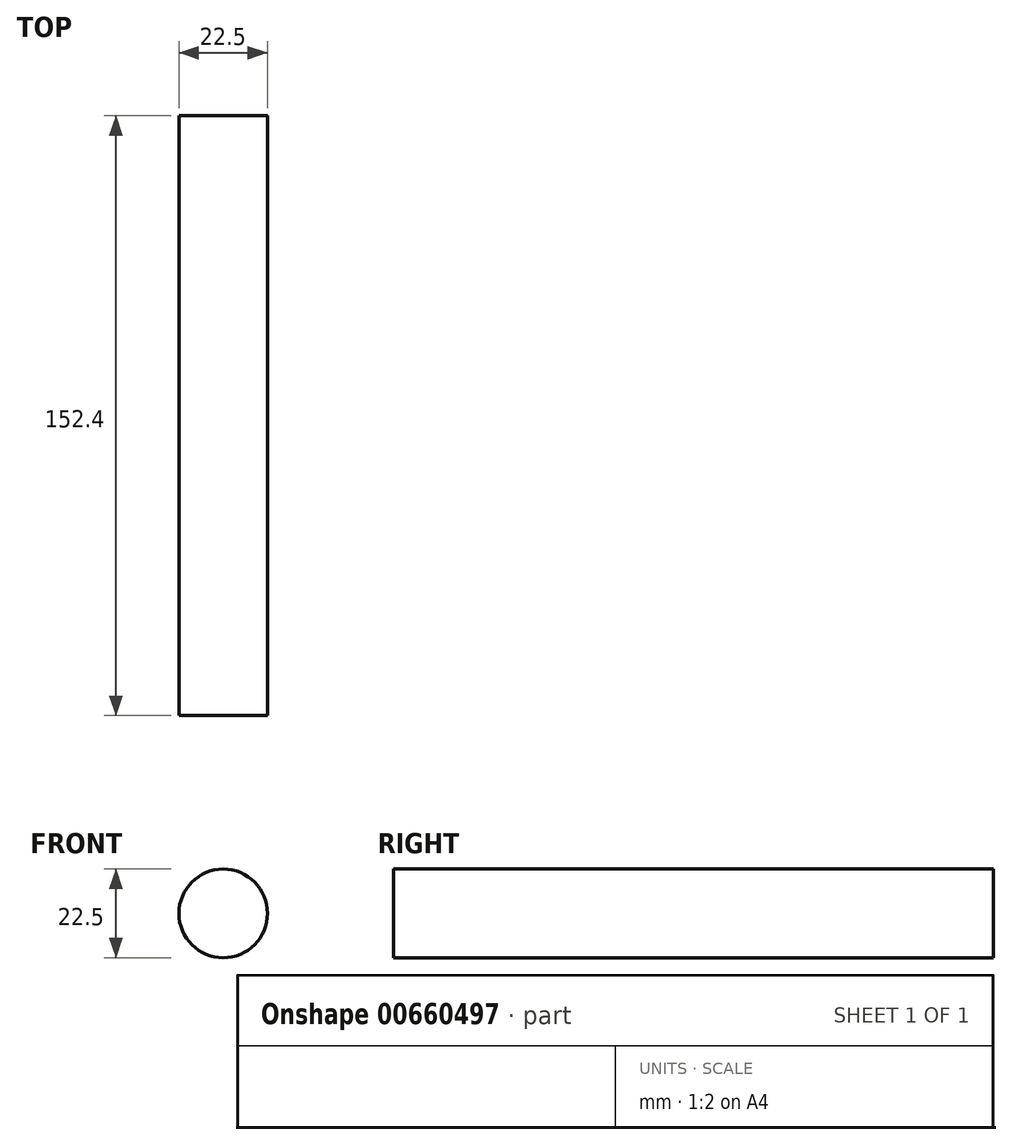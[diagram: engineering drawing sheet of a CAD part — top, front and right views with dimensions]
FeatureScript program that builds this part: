
annotation { "Feature Type Name" : "Feature", "Feature Type Description" : "" }
export const myFeature = defineFeature(function(context is Context, id is Id, definition is map)
    precondition{}
    {
        {
            var Q0;
            Q0=qCreatedBy(makeId("Front.planeOp"),FACE);
            var sketch = newSketch(context, id + "F0", { "sketchPlane" : qUnion([Q0])});
            skCircle(sketch, "E0", {"center": v(0, 0) * mm, "radius": 11.25 * mm});
            skSolve(sketch);
        }
        {
            var Q0;
            Q0=makeQuery(id+"F0.imprint","IMPRINT",FACE,{"disambiguationData":[TD([[makeQuery(id+"F0.imprint","IMPRINT",EDGE,{"derivedFrom":sQuery(id+"F0.wireOp",EDGE,"E0")}),1.0]])]});
            extrude(context, id + "F1", {"entities" : qUnion([Q0]), "depth" : 152.4 * mm, "offsetDistance" : 25.4 * mm});
        }
    });
